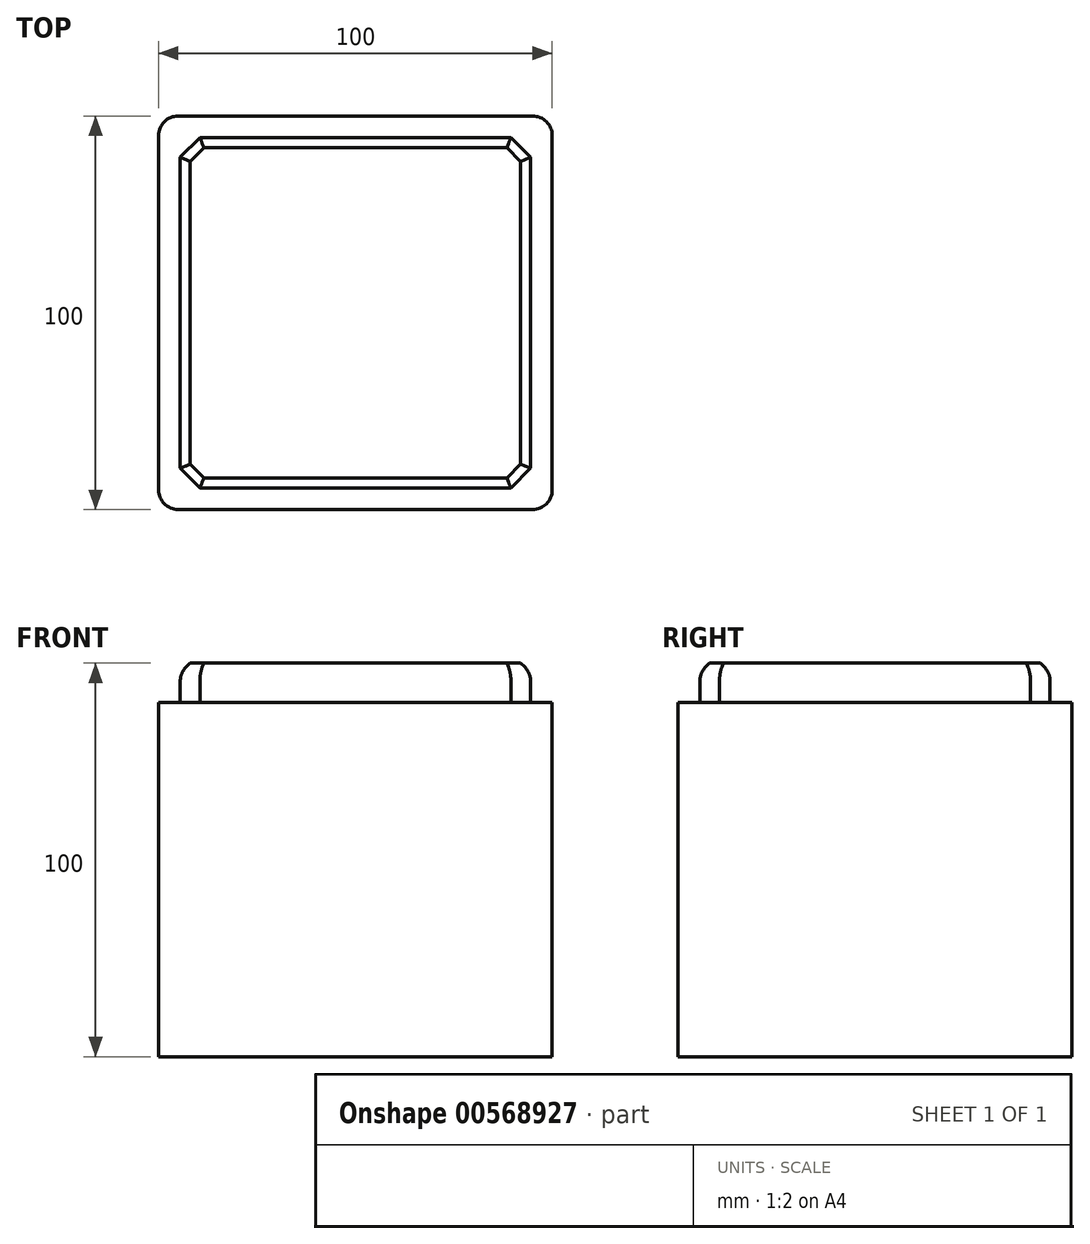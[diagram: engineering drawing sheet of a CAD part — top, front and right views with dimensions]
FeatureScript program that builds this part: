
annotation { "Feature Type Name" : "Feature", "Feature Type Description" : "" }
export const myFeature = defineFeature(function(context is Context, id is Id, definition is map)
    precondition{}
    {
        {
            var Q0;
            Q0=qCreatedBy(makeId("Top.planeOp"),FACE);
            var sketch = newSketch(context, id + "F0", { "sketchPlane" : qUnion([Q0])});
            skLineSegment(sketch, "E0.bottom", {"start": v(-45, 50) * mm, "end": v(45, 50) * mm});
            skLineSegment(sketch, "E0.top", {"start": v(-45, -50) * mm, "end": v(45, -50) * mm});
            skLineSegment(sketch, "E0.left", {"start": v(-50, 45) * mm, "end": v(-50, -45) * mm});
            skLineSegment(sketch, "E0.right", {"start": v(50, 45) * mm, "end": v(50, -45) * mm});
            skPoint(sketch, "E0.middle", {"position": v(0, 0) * mm});
            skPoint(sketch, "E1.visualSharp", {"position": v(-50, 50) * mm});
            skArc(sketch, "E1.filletArc", {"start": v(-45, 50) * mm, "mid": v(-48.54, 48.54) * mm, "end": v(-50, 45) * mm});
            skPoint(sketch, "E2.visualSharp", {"position": v(-50, -50) * mm});
            skArc(sketch, "E2.filletArc", {"start": v(-50, -45) * mm, "mid": v(-48.54, -48.54) * mm, "end": v(-45, -50) * mm});
            skPoint(sketch, "E3.visualSharp", {"position": v(50, -50) * mm});
            skArc(sketch, "E3.filletArc", {"start": v(45, -50) * mm, "mid": v(48.54, -48.54) * mm, "end": v(50, -45) * mm});
            skPoint(sketch, "E4.visualSharp", {"position": v(50, 50) * mm});
            skArc(sketch, "E4.filletArc", {"start": v(50, 45) * mm, "mid": v(48.54, 48.54) * mm, "end": v(45, 50) * mm});
            skSolve(sketch);
        }
        {
            var Q0;
            Q0 = qSketchRegion(id + "F0", true);
            extrude(context, id + "F1", {"entities" : qUnion([Q0]), "flatOperationType" : FlatOperationType.REMOVE, "depth" : 90 * mm, "offsetDistance" : 25 * mm, "domain" : OperationDomain.MODEL});
        }
        {
            var Q0;
            Q0=makeQuery(id+"F1.opExtrude","CAP_FACE",FACE,{"disambiguationData":[OSD([sQuery(id+"F0.wireOp",EDGE,"E0.bottom"),sQuery(id+"F0.wireOp",EDGE,"E0.top"),sQuery(id+"F0.wireOp",EDGE,"E0.left"),sQuery(id+"F0.wireOp",EDGE,"E0.right"),sQuery(id+"F0.wireOp",EDGE,"E1.filletArc"),sQuery(id+"F0.wireOp",EDGE,"E2.filletArc"),sQuery(id+"F0.wireOp",EDGE,"E3.filletArc"),sQuery(id+"F0.wireOp",EDGE,"E4.filletArc")])],"isStart":false});
            var sketch = newSketch(context, id + "F2", { "sketchPlane" : qUnion([Q0])});
            skSolve(sketch);
        }
        {
            var Q0;
            Q0=makeQuery(id+"F2.imprint","IMPRINT",FACE,{"disambiguationData":[TD([[makeQuery(id+"F2.imprint","IMPRINT",EDGE,{"derivedFrom":makeQuery(id+"F1.opExtrude","CAP_EDGE",EDGE,{"disambiguationData":[OSD([sQuery(id+"F0.wireOp",EDGE,"E0.bottom")])],"isStart":false})}),-1.0]])]});
            var sketch = newSketch(context, id + "F3", { "sketchPlane" : qUnion([Q0])});
            skLineSegment(sketch, "E5.0", {"start": v(-44.5, 44.5) * mm, "end": v(-44.5, -44.5) * mm});
            skLineSegment(sketch, "E5.1", {"start": v(44.5, 44.5) * mm, "end": v(-44.5, 44.5) * mm});
            skLineSegment(sketch, "E5.2", {"start": v(44.5, -44.5) * mm, "end": v(44.5, 44.5) * mm});
            skLineSegment(sketch, "E5.3", {"start": v(-44.5, -44.5) * mm, "end": v(44.5, -44.5) * mm});
            skSolve(sketch);
        }
        {
            var Q0;
            Q0 = qSketchRegion(id + "F3", true);
            extrude(context, id + "F4", {"entities" : qUnion([Q0]), "operationType" : NewBodyOperationType.ADD, "flatOperationType" : FlatOperationType.REMOVE, "depth" : 10 * mm, "offsetDistance" : 25 * mm, "domain" : OperationDomain.MODEL});
        }
        {
            var Q0;
            Q0=makeQuery(id+"F4.opExtrude","SWEPT_EDGE",EDGE,{"disambiguationData":[OSD([sQuery(id+"F3.wireOp",EDGE,"E5.2"),sQuery(id+"F3.wireOp",EDGE,"E5.3")])]});
            var Q1;
            Q1=makeQuery(id+"F4.opExtrude","SWEPT_EDGE",EDGE,{"disambiguationData":[OSD([sQuery(id+"F3.wireOp",EDGE,"E5.0"),sQuery(id+"F3.wireOp",EDGE,"E5.3")])]});
            var Q2;
            Q2=makeQuery(id+"F4.opExtrude","SWEPT_EDGE",EDGE,{"disambiguationData":[OSD([sQuery(id+"F3.wireOp",EDGE,"E5.1"),sQuery(id+"F3.wireOp",EDGE,"E5.2")])]});
            var Q3;
            Q3=makeQuery(id+"F4.opExtrude","SWEPT_EDGE",EDGE,{"disambiguationData":[OSD([sQuery(id+"F3.wireOp",EDGE,"E5.0"),sQuery(id+"F3.wireOp",EDGE,"E5.1")])]});
            chamfer(context, id + "F5", {"entities" : qUnion([Q0, Q1, Q2, Q3]), "width" : 5 * mm, "tangentPropagation" : true});
        }
        {
            var Q0;
            Q0=makeQuery(id+"F4.opExtrude","CAP_FACE",FACE,{"disambiguationData":[OSD([sQuery(id+"F3.wireOp",EDGE,"E5.0"),sQuery(id+"F3.wireOp",EDGE,"E5.1"),sQuery(id+"F3.wireOp",EDGE,"E5.2"),sQuery(id+"F3.wireOp",EDGE,"E5.3")])],"isStart":false});
            chamfer(context, id + "F6", {"entities" : qUnion([Q0]), "width" : 2.5 * mm, "tangentPropagation" : true});
        }
        {
            var Q0;
            {var subQ0=sQuery(id+"F3.wireOp",EDGE,"E5.0");Q0=makeQuery(id+"F6.opChamfer","BLEND_EDGE",EDGE,{"blendedFrom":[makeQuery(id+"F4.opExtrude","CAP_EDGE",EDGE,{"disambiguationData":[OSD([subQ0])],"isStart":false}),makeQuery(id+"F4.opExtrude","SWEPT_FACE",FACE,{"disambiguationData":[OSD([subQ0])]})],"blendedInto":[makeQuery(id+"F4.opExtrude","SWEPT_FACE",FACE,{"disambiguationData":[OSD([subQ0])]})]});}
            var Q1;
            {var subQ0=sQuery(id+"F3.wireOp",EDGE,"E5.3");var subQ1=sQuery(id+"F3.wireOp",EDGE,"E5.0");Q1=makeQuery(id+"F6.opChamfer","BLEND_EDGE",EDGE,{"blendedFrom":[makeQuery(id+"F5.opChamfer","BLEND_EDGE",EDGE,{"blendedFrom":[makeQuery(id+"F4.opExtrude","SWEPT_EDGE",EDGE,{"disambiguationData":[OSD([subQ1,subQ0])]}),makeQuery(id+"F4.opExtrude","CAP_FACE",FACE,{"disambiguationData":[OSD([subQ1,sQuery(id+"F3.wireOp",EDGE,"E5.1"),sQuery(id+"F3.wireOp",EDGE,"E5.2"),subQ0])],"isStart":false})],"blendedInto":[makeQuery(id+"F4.opExtrude","CAP_FACE",FACE,{"disambiguationData":[OSD([subQ1,sQuery(id+"F3.wireOp",EDGE,"E5.1"),sQuery(id+"F3.wireOp",EDGE,"E5.2"),subQ0])],"isStart":false})]}),makeQuery(id+"F5.opChamfer","BLEND_FACE",FACE,{"disambiguationData":[OSD([subQ1,subQ0])]})],"blendedInto":[makeQuery(id+"F5.opChamfer","BLEND_FACE",FACE,{"disambiguationData":[OSD([subQ1,subQ0])]})]});}
            var Q2;
            {var subQ0=sQuery(id+"F3.wireOp",EDGE,"E5.3");Q2=makeQuery(id+"F6.opChamfer","BLEND_EDGE",EDGE,{"blendedFrom":[makeQuery(id+"F4.opExtrude","CAP_EDGE",EDGE,{"disambiguationData":[OSD([subQ0])],"isStart":false}),makeQuery(id+"F4.opExtrude","SWEPT_FACE",FACE,{"disambiguationData":[OSD([subQ0])]})],"blendedInto":[makeQuery(id+"F4.opExtrude","SWEPT_FACE",FACE,{"disambiguationData":[OSD([subQ0])]})]});}
            var Q3;
            {var subQ0=sQuery(id+"F3.wireOp",EDGE,"E5.1");var subQ1=sQuery(id+"F3.wireOp",EDGE,"E5.0");Q3=makeQuery(id+"F6.opChamfer","BLEND_EDGE",EDGE,{"blendedFrom":[makeQuery(id+"F5.opChamfer","BLEND_EDGE",EDGE,{"blendedFrom":[makeQuery(id+"F4.opExtrude","SWEPT_EDGE",EDGE,{"disambiguationData":[OSD([subQ1,subQ0])]}),makeQuery(id+"F4.opExtrude","CAP_FACE",FACE,{"disambiguationData":[OSD([subQ1,subQ0,sQuery(id+"F3.wireOp",EDGE,"E5.2"),sQuery(id+"F3.wireOp",EDGE,"E5.3")])],"isStart":false})],"blendedInto":[makeQuery(id+"F4.opExtrude","CAP_FACE",FACE,{"disambiguationData":[OSD([subQ1,subQ0,sQuery(id+"F3.wireOp",EDGE,"E5.2"),sQuery(id+"F3.wireOp",EDGE,"E5.3")])],"isStart":false})]}),makeQuery(id+"F5.opChamfer","BLEND_FACE",FACE,{"disambiguationData":[OSD([subQ1,subQ0])]})],"blendedInto":[makeQuery(id+"F5.opChamfer","BLEND_FACE",FACE,{"disambiguationData":[OSD([subQ1,subQ0])]})]});}
            var Q4;
            {var subQ0=sQuery(id+"F3.wireOp",EDGE,"E5.1");Q4=makeQuery(id+"F6.opChamfer","BLEND_EDGE",EDGE,{"blendedFrom":[makeQuery(id+"F4.opExtrude","CAP_EDGE",EDGE,{"disambiguationData":[OSD([subQ0])],"isStart":false}),makeQuery(id+"F4.opExtrude","SWEPT_FACE",FACE,{"disambiguationData":[OSD([subQ0])]})],"blendedInto":[makeQuery(id+"F4.opExtrude","SWEPT_FACE",FACE,{"disambiguationData":[OSD([subQ0])]})]});}
            var Q5;
            {var subQ0=sQuery(id+"F3.wireOp",EDGE,"E5.2");var subQ1=sQuery(id+"F3.wireOp",EDGE,"E5.1");Q5=makeQuery(id+"F6.opChamfer","BLEND_EDGE",EDGE,{"blendedFrom":[makeQuery(id+"F5.opChamfer","BLEND_EDGE",EDGE,{"blendedFrom":[makeQuery(id+"F4.opExtrude","SWEPT_EDGE",EDGE,{"disambiguationData":[OSD([subQ1,subQ0])]}),makeQuery(id+"F4.opExtrude","CAP_FACE",FACE,{"disambiguationData":[OSD([sQuery(id+"F3.wireOp",EDGE,"E5.0"),subQ1,subQ0,sQuery(id+"F3.wireOp",EDGE,"E5.3")])],"isStart":false})],"blendedInto":[makeQuery(id+"F4.opExtrude","CAP_FACE",FACE,{"disambiguationData":[OSD([sQuery(id+"F3.wireOp",EDGE,"E5.0"),subQ1,subQ0,sQuery(id+"F3.wireOp",EDGE,"E5.3")])],"isStart":false})]}),makeQuery(id+"F5.opChamfer","BLEND_FACE",FACE,{"disambiguationData":[OSD([subQ1,subQ0])]})],"blendedInto":[makeQuery(id+"F5.opChamfer","BLEND_FACE",FACE,{"disambiguationData":[OSD([subQ1,subQ0])]})]});}
            var Q6;
            {var subQ0=sQuery(id+"F3.wireOp",EDGE,"E5.2");Q6=makeQuery(id+"F6.opChamfer","BLEND_EDGE",EDGE,{"blendedFrom":[makeQuery(id+"F4.opExtrude","CAP_EDGE",EDGE,{"disambiguationData":[OSD([subQ0])],"isStart":false}),makeQuery(id+"F4.opExtrude","SWEPT_FACE",FACE,{"disambiguationData":[OSD([subQ0])]})],"blendedInto":[makeQuery(id+"F4.opExtrude","SWEPT_FACE",FACE,{"disambiguationData":[OSD([subQ0])]})]});}
            var Q7;
            {var subQ0=sQuery(id+"F3.wireOp",EDGE,"E5.3");var subQ1=sQuery(id+"F3.wireOp",EDGE,"E5.2");Q7=makeQuery(id+"F6.opChamfer","BLEND_EDGE",EDGE,{"blendedFrom":[makeQuery(id+"F5.opChamfer","BLEND_EDGE",EDGE,{"blendedFrom":[makeQuery(id+"F4.opExtrude","SWEPT_EDGE",EDGE,{"disambiguationData":[OSD([subQ1,subQ0])]}),makeQuery(id+"F4.opExtrude","CAP_FACE",FACE,{"disambiguationData":[OSD([sQuery(id+"F3.wireOp",EDGE,"E5.0"),sQuery(id+"F3.wireOp",EDGE,"E5.1"),subQ1,subQ0])],"isStart":false})],"blendedInto":[makeQuery(id+"F4.opExtrude","CAP_FACE",FACE,{"disambiguationData":[OSD([sQuery(id+"F3.wireOp",EDGE,"E5.0"),sQuery(id+"F3.wireOp",EDGE,"E5.1"),subQ1,subQ0])],"isStart":false})]}),makeQuery(id+"F5.opChamfer","BLEND_FACE",FACE,{"disambiguationData":[OSD([subQ1,subQ0])]})],"blendedInto":[makeQuery(id+"F5.opChamfer","BLEND_FACE",FACE,{"disambiguationData":[OSD([subQ1,subQ0])]})]});}
            fillet(context, id + "F7", {"entities" : qUnion([Q0, Q1, Q2, Q3, Q4, Q5, Q6, Q7]), "radius" : 5 * mm, "tangentPropagation" : true, "allowEdgeOverflow" : false});
        }
    });
